# Revit family: Shower-Bath_Shower-STERLING-Performa-71040110
name_source: partatom
category: Plumbing Fixtures
revit_build: Autodesk Revit 2015 (Build: 20140606_1530(x64)
units: mm (PartAtom-declared; Revit-internal decimal feet)

## types (2) — shared parameters
ADA = No
Assembly Code = D2010500
CW Connection = No
Cold Water Inlet = Cold Water Inlet
Date Modified = 01/16/2018
Default Elevation = 0"
Description = Performa™ Series 7104, 60 inch x 30 inch Bath/Shower
HW Connection = No
Height = 76 1/2"
Hot Water Inlet = Hot Water Inlet
Length = 60"
Manufacturer = KOHLER Co.
MasterFormat 1995 = 15410
MasterFormat 2004 = 22.41.19
Material = Solid Vikrell
Product Documentation Link = https://resources.kohler.com
Product Name = Performa
Product Page URL = http://www.sterlingplumbing.com
URL = https://www.sterlingplumbing.com
Vent Connection = No
Waste Connection = Yes
Waste Water Outlet = Waste Water Outlet
Width = 29 7/32"

## per-type parameters (varying)
| type | Finish | Model | Type |
| 0-White | Kohler-Vikrell-0-White | 71040110-0 | 1 |
| 96-Biscuit | Kohler-Vikrell-96-Biscuit | 71040110-96 | 2 |

## geometry (parser evidence)
native form markers: Sweep x5
no freeform markers — native parametric forms only
